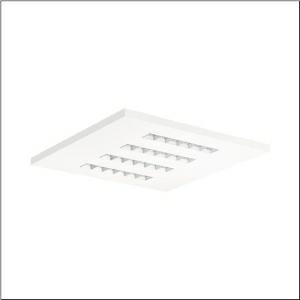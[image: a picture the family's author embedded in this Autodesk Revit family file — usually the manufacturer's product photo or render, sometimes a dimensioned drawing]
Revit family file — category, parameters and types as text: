
# Revit family: silica_21_square_51mx6mtst4w
name_source: partatom
category: Lighting Fixtures
units: mm (PartAtom-declared; Revit-internal decimal feet)

## family parameters
Cut with Voids When Loaded = No
Host = Face
Light Source = No
Part Type = Normal
Room Calculation Point = No
Round Connector Dimension = Use Diameter
Shared = No

## types (1)
- --- (1 x LED 2700 K ... 6500 K, 3720 lm, 30.7 W, 6500K)
    Apparent Load = 31 VA
    CIE Flux Codes = 81 98 100 100 100
    Color Rendering = 80
    Color Temperature = 6500K
    Default Elevation = 1800 mm
    Description = Silica 21 Square, office luminaire, primary light control with lens, of PMMA, primary anti-glare with reflector, of PC, white, CAT 2 (L<= 3000cd/m²), light emission: direct distribution, primary light characteristic: symmetric, installation type: lay-in mounting, LED, rated luminous flux: 3.720lm, luminous efficacy: 113lm/W, light colour: 8tw, colour temperature: 2700..6500K, control gear: DALI-2 DT8, with terminal, 5-pole, mains connection: 220..240V, AC, 50/60Hz, rated input power: 32.8W, luminaire housing, of aluminium, traffic white (RAL 9016), module: M600, length: 600mm, width: 600mm, height: 32mm, protection rating (complete): IP20, insulation class (complete): insulation class I (protective earthing), certification: CE, ENEC, VDE, permissible operating ambient temperature: 0..+35°C, standard: EN 50419, packaging unit: 1 piece
    Height = 0 mm  [stored 0 ft]
    Lamp = 1 x LED 2700 K ... 6500 K
    Lamp Light Flux = 3720 lm
    Lamp Power = 30.7 W
    Lamp count = 1
    Length = 597 mm
    Luminous efficacy = 121 lm/W
    Manufacturer = Siteco
    ModVariant = No
    Model = 51MX6MTST4W
    Mounting Place = Ceiling
    Mounting Type = Recessed
    Number of Poles = 1
    OnlyDefault = Yes
    Power Factor = 1
    Product Name = Silica 21 Square
    Product group = office luminaire | ceiling recessed
    ProductGroupID = 400
    Protection Class = Protection class I
    Protection Degree = IP 20
    RLX_Detail_Level = 1
    RLX_Emergency_Light_Flux = 0 lm
    RLX_Emergency_Type = 0
    RLX_Emergency_Type_DB = No
    RlxData = <blob elided: 22449 chars, md5=00be9b7a>
    Socket = socket
    Standby Power = 0 W
    System Light Flux = 3720 lm
    System Power = 31 W
    Type Comments = individual setting: CCT=6500K, colour temperature 6500K, luminous flux: 100 % | dim-lin: 254 | 381 mA
    Type Image = l_1275220.jpg
    URL = http://relux.com
    VarID = @adj_071331
    Voltage = 0 V
    Weight = 0.00 kg
    Width = 597 mm

note: [stored X ft] marks values corroborated as IEEE doubles in the binary element streams (Revit-internal decimal feet)

## geometry (parser evidence)
native form markers: Blend x4, Sweep x10
no freeform markers — native parametric forms only
